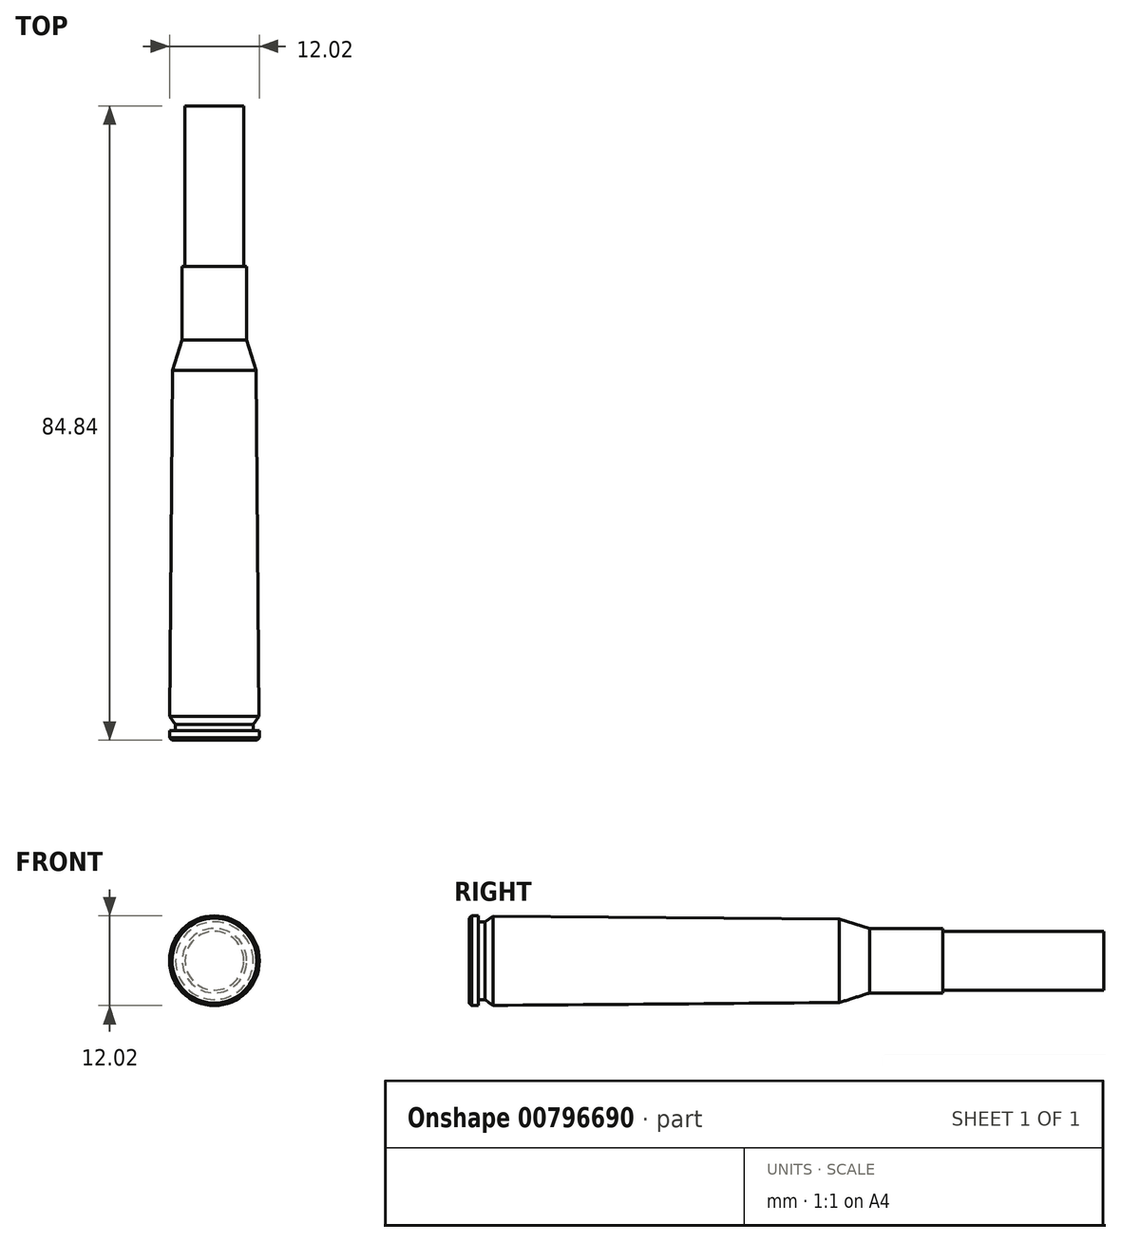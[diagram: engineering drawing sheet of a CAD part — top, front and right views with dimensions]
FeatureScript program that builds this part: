
annotation { "Feature Type Name" : "Feature", "Feature Type Description" : "" }
export const myFeature = defineFeature(function(context is Context, id is Id, definition is map)
    precondition{}
    {
        {
            var Q0;
            Q0=qCreatedBy(makeId("Right.planeOp"),FACE);
            var sketch = newSketch(context, id + "F0", { "sketchPlane" : qUnion([Q0])});
            skLineSegment(sketch, "E0", {"start": v(0, 0) * mm, "end": v(0.33, 0) * mm});
            skLineSegment(sketch, "E1", {"start": v(0, -6.81) * mm, "end": v(1.24, -6.81) * mm});
            skLineSegment(sketch, "E2", {"start": v(0, -4.96) * mm, "end": v(3.16, -4.96) * mm});
            skLineSegment(sketch, "E3", {"start": v(0, -8.65) * mm, "end": v(49.5, -8.65) * mm});
            skLineSegment(sketch, "E4", {"start": v(0, -12.59) * mm, "end": v(53.56, -12.59) * mm});
            skLineSegment(sketch, "E5", {"start": v(0, -18.69) * mm, "end": v(63.35, -18.69) * mm});
            skLineSegment(sketch, "E6", {"start": v(0, -25) * mm, "end": v(84.84, -25) * mm});
            skLineSegment(sketch, "E7", {"start": v(0.33, 0) * mm, "end": v(1.24, 0) * mm});
            skLineSegment(sketch, "E8", {"start": v(1.24, 0) * mm, "end": v(2.08, 0) * mm});
            skLineSegment(sketch, "E9", {"start": v(2.08, 0) * mm, "end": v(3.16, 0) * mm});
            skLineSegment(sketch, "E10", {"start": v(3.16, 0) * mm, "end": v(49.5, 0) * mm});
            skLineSegment(sketch, "E11", {"start": v(49.5, 0) * mm, "end": v(53.56, 0) * mm});
            skLineSegment(sketch, "E12", {"start": v(53.56, 0) * mm, "end": v(63.35, 0) * mm});
            skLineSegment(sketch, "E13", {"start": v(63.35, 0) * mm, "end": v(84.84, 0) * mm});
            skLineSegment(sketch, "E14", {"start": v(84.84, 0) * mm, "end": v(84.84, 3.92) * mm});
            skLineSegment(sketch, "E15", {"start": v(84.84, 3.92) * mm, "end": v(63.35, 3.92) * mm});
            skLineSegment(sketch, "E16", {"start": v(63.35, 0) * mm, "end": v(63.35, 4.32) * mm});
            skLineSegment(sketch, "E17", {"start": v(63.35, 4.32) * mm, "end": v(53.56, 4.32) * mm});
            skLineSegment(sketch, "E18", {"start": v(53.56, 4.32) * mm, "end": v(49.5, 5.6) * mm});
            skLineSegment(sketch, "E19", {"start": v(49.5, 5.6) * mm, "end": v(49.5, 0) * mm});
            skLineSegment(sketch, "E20", {"start": v(49.5, 5.6) * mm, "end": v(3.16, 5.98) * mm});
            skLineSegment(sketch, "E21", {"start": v(3.16, 5.98) * mm, "end": v(3.16, 0) * mm});
            skLineSegment(sketch, "E22", {"start": v(2.08, 0) * mm, "end": v(2.08, 5.2) * mm});
            skLineSegment(sketch, "E23", {"start": v(2.08, 5.2) * mm, "end": v(3.16, 5.98) * mm});
            skLineSegment(sketch, "E24", {"start": v(2.08, 5.2) * mm, "end": v(1.24, 5.2) * mm});
            skLineSegment(sketch, "E25", {"start": v(0.33, 6) * mm, "end": v(0.33, 0) * mm});
            skLineSegment(sketch, "E26", {"start": v(0.33, 6) * mm, "end": v(0, 5.67) * mm});
            skLineSegment(sketch, "E27", {"start": v(0, 5.67) * mm, "end": v(0, 0) * mm});
            skLineSegment(sketch, "E28", {"start": v(0.33, 6) * mm, "end": v(1.24, 6) * mm});
            skLineSegment(sketch, "E29", {"start": v(1.24, 6) * mm, "end": v(1.24, 5.2) * mm});
            skSolve(sketch);
        }
        {
            var Q0;
            Q0=makeQuery(id+"F0.imprint","IMPRINT",FACE,{"disambiguationData":[TD([[makeQuery(id+"F0.imprint","IMPRINT",EDGE,{"derivedFrom":sQuery(id+"F0.wireOp",EDGE,"E0")}),1.0]])]});
            var Q1;
            Q1=makeQuery(id+"F0.imprint","IMPRINT",FACE,{"disambiguationData":[TD([[makeQuery(id+"F0.imprint","IMPRINT",EDGE,{"derivedFrom":sQuery(id+"F0.wireOp",EDGE,"E7")}),1.0]])]});
            var Q2;
            Q2=makeQuery(id+"F0.imprint","IMPRINT",FACE,{"disambiguationData":[TD([[makeQuery(id+"F0.imprint","IMPRINT",EDGE,{"derivedFrom":sQuery(id+"F0.wireOp",EDGE,"E9")}),1.0]])]});
            var Q3;
            Q3=makeQuery(id+"F0.imprint","IMPRINT",FACE,{"disambiguationData":[TD([[makeQuery(id+"F0.imprint","IMPRINT",EDGE,{"derivedFrom":sQuery(id+"F0.wireOp",EDGE,"E10")}),1.0]])]});
            var Q4;
            Q4=makeQuery(id+"F0.imprint","IMPRINT",FACE,{"disambiguationData":[TD([[makeQuery(id+"F0.imprint","IMPRINT",EDGE,{"derivedFrom":sQuery(id+"F0.wireOp",EDGE,"E11")}),1.0]])]});
            var Q5;
            {var subQ0=sQuery(id+"F0.wireOp",EDGE,"E13");Q5=makeQuery(id+"F0.imprint","IMPRINT",FACE,{"disambiguationData":[TD([[makeQuery(id+"F0.imprint","IMPRINT",EDGE,{"derivedFrom":subQ0}),1.0]])]});}
            var Q6;
            Q6=sQuery(id+"F0.wireOp",EDGE,"E10");
            revolve(context, id + "F1", {"surfaceOperationType" : NewSurfaceOperationType.NEW, "entities" : qUnion([Q0, Q1, Q2, Q3, Q4, Q5]), "axis" : qUnion([Q6]), "revolveType" : RevolveType.FULL});
        }
    });
